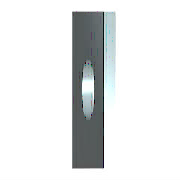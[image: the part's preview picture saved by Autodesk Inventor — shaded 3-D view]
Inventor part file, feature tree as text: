
AUTODESK INVENTOR PART (.ipt)
format: ipt  version: 2013 (Build 170138000, 138)  size: 101,376 bytes
history: native  units: mm (DEFAULTED — no unit token found)
features: sketch x1, other x1, plane x1
ambient origin geometry x7: Origin, YZ Plane, XY Plane, X Axis, Y Axis, Z Axis, Center Point
bodies: Solid1 (feature_tree), Body (feature_tree)
feature tree (3):
  sketch  "Sketch1"  dims[d0=10.8mm d1=10.8mm d2=1.5mm d3=0.0mm d4=4.05mm d5=6.0mm d6=4.0mm d7=2.0mm d8=14.3117mm d9=8.0mm d10=20.594885mm d11=0.0mm d12=0.0mm d13=0.0mm d14=90.0deg d15=0.0mm]
  other  "Work Axis1"
  plane  "Work Plane1"
